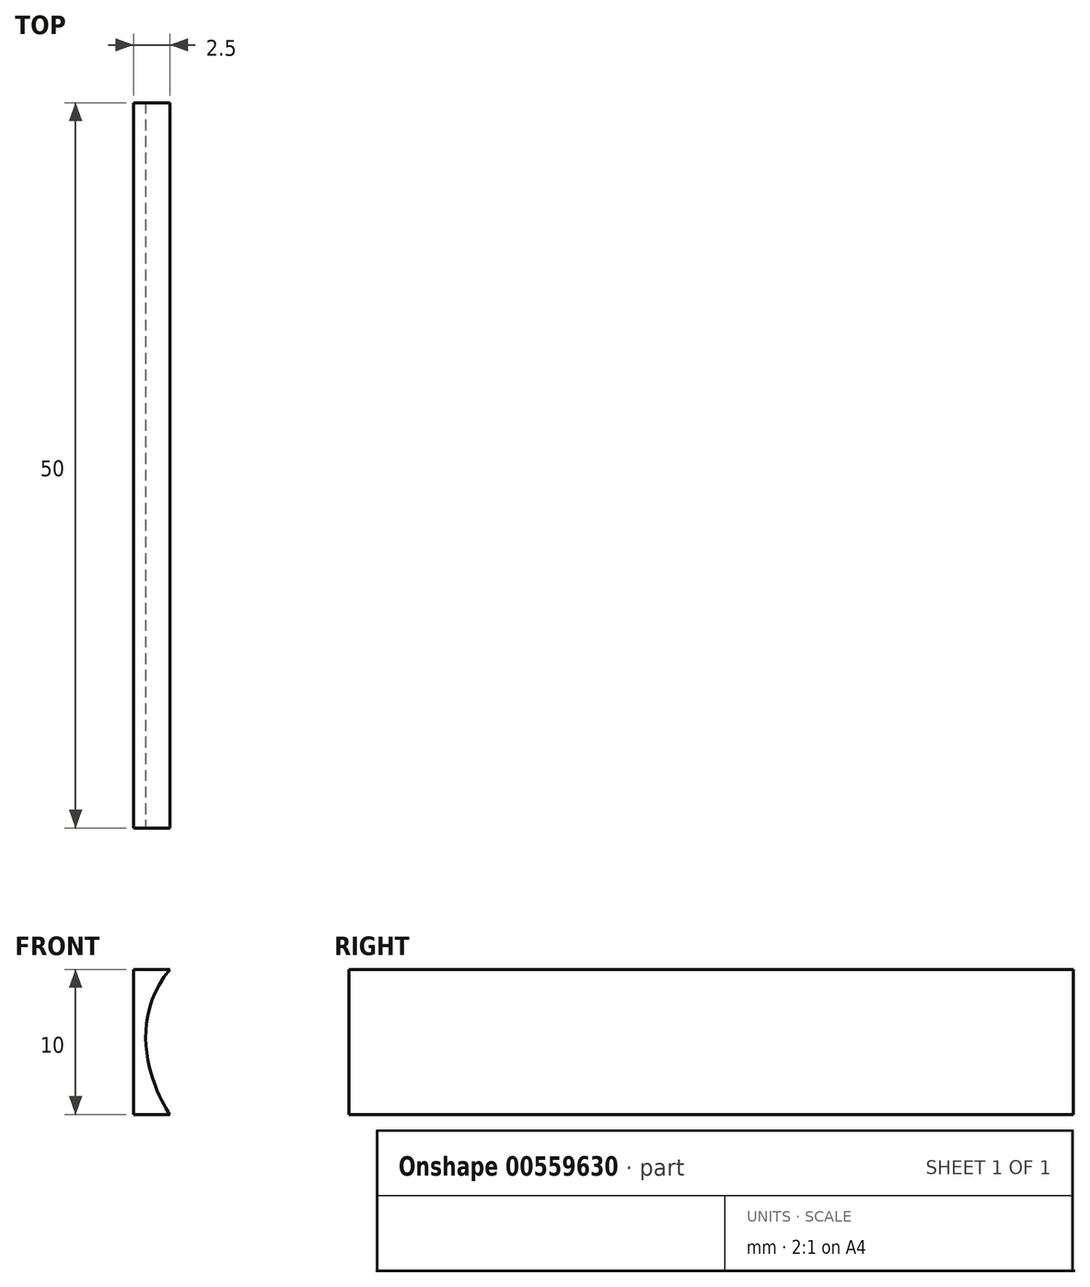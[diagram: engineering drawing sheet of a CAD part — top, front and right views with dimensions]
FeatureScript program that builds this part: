
annotation { "Feature Type Name" : "Feature", "Feature Type Description" : "" }
export const myFeature = defineFeature(function(context is Context, id is Id, definition is map)
    precondition{}
    {
        {
            var Q0;
            Q0=qCreatedBy(makeId("Front.planeOp"),FACE);
            var sketch = newSketch(context, id + "F0", { "sketchPlane" : qUnion([Q0])});
            skLineSegment(sketch, "E0.bottom", {"start": v(0, 0) * mm, "end": v(2.5, 0) * mm});
            skLineSegment(sketch, "E0.top", {"start": v(0, 10) * mm, "end": v(2.5, 10) * mm});
            skLineSegment(sketch, "E0.left", {"start": v(0, 0) * mm, "end": v(0, 10) * mm});
            skFitSpline(sketch, "E1", {"points": [v(2.5, 10) * mm, v(2.5, 0) * mm], "startDerivative": vector(-9.72, -11.93) * mm, "endDerivative": vector(2.67, -3.97) * mm});
            skSolve(sketch);
        }
        {
            var Q0;
            Q0 = qSketchRegion(id + "F0", true);
            extrude(context, id + "F1", {"entities" : qUnion([Q0]), "depth" : 50 * mm, "offsetDistance" : 25 * mm});
        }
    });
